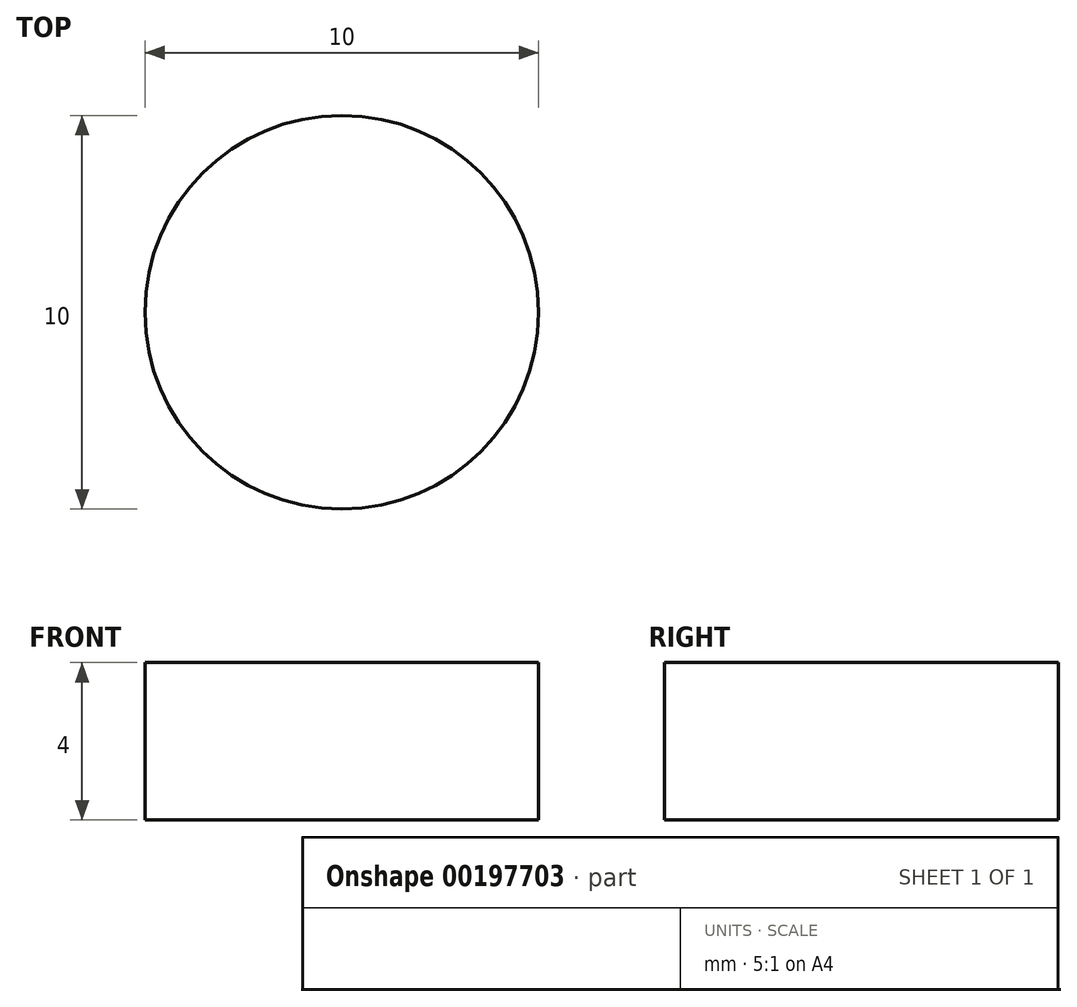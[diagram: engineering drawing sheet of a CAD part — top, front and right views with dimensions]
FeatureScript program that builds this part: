
annotation { "Feature Type Name" : "Feature", "Feature Type Description" : "" }
export const myFeature = defineFeature(function(context is Context, id is Id, definition is map)
    precondition{}
    {
        {
            var Q0;
            Q0=qCreatedBy(makeId("Top.planeOp"),FACE);
            var sketch = newSketch(context, id + "F0", { "sketchPlane" : qUnion([Q0])});
            skCircle(sketch, "E0", {"center": v(0, 0) * mm, "radius": 5 * mm});
            skSolve(sketch);
        }
        {
            var Q0;
            Q0 = qSketchRegion(id + "F0", true);
            extrude(context, id + "F1", {"entities" : qUnion([Q0]), "depth" : 4 * mm});
        }
    });
